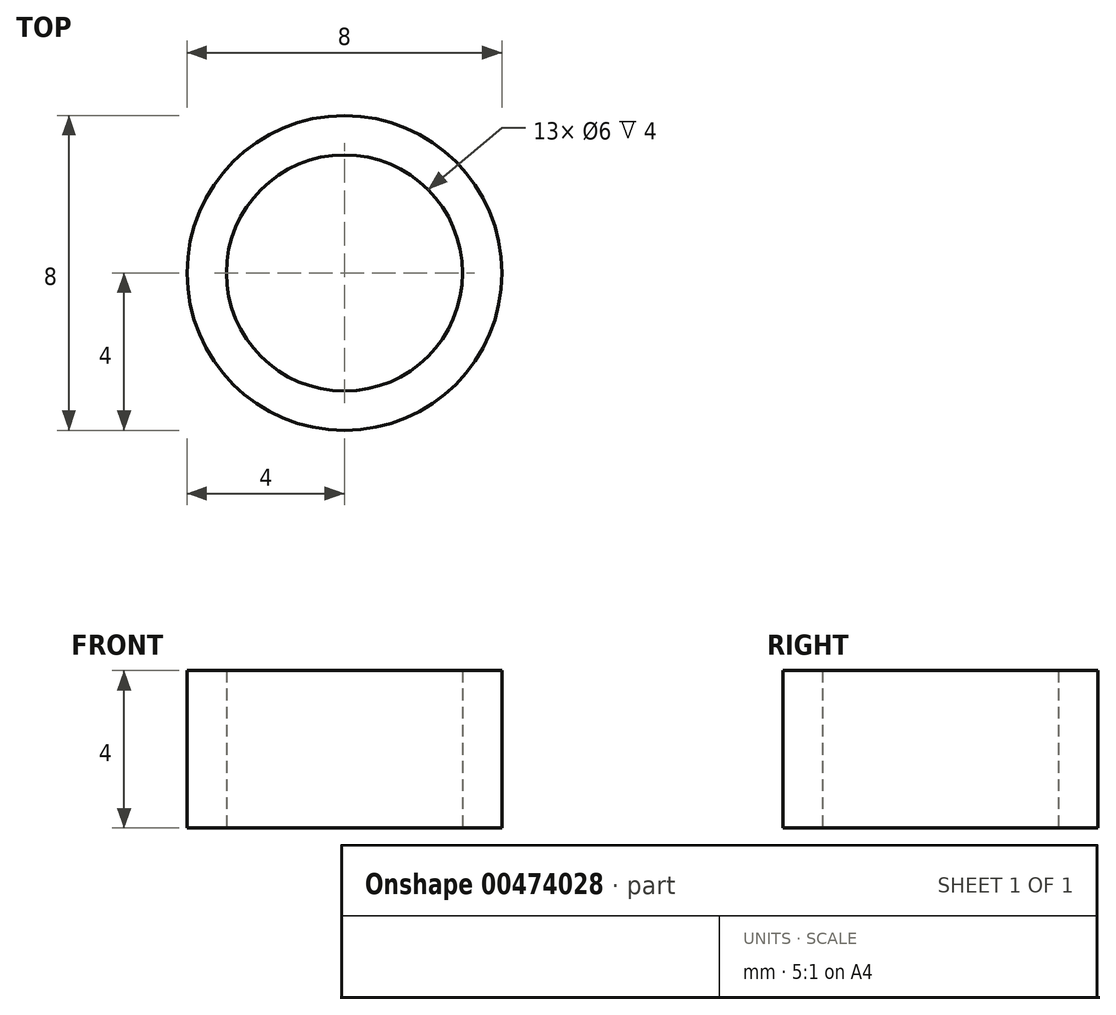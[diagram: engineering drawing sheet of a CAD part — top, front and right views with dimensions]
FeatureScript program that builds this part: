
annotation { "Feature Type Name" : "Feature", "Feature Type Description" : "" }
export const myFeature = defineFeature(function(context is Context, id is Id, definition is map)
    precondition{}
    {
        {
            var Q0;
            Q0=qCreatedBy(makeId("Top.planeOp"),FACE);
            var sketch = newSketch(context, id + "F0", { "sketchPlane" : qUnion([Q0])});
            skCircle(sketch, "E0", {"center": v(0, 0) * mm, "radius": 4 * mm});
            skCircle(sketch, "E1", {"center": v(0, 0) * mm, "radius": 3 * mm});
            skSolve(sketch);
        }
        {
            var Q0;
            Q0=makeQuery(id+"F0.imprint","IMPRINT",FACE,{"disambiguationData":[TD([[makeQuery(id+"F0.imprint","IMPRINT",EDGE,{"derivedFrom":sQuery(id+"F0.wireOp",EDGE,"E0")}),1.0]])]});
            extrude(context, id + "F1", {"entities" : qUnion([Q0]), "depth" : 4 * mm});
        }
    });
